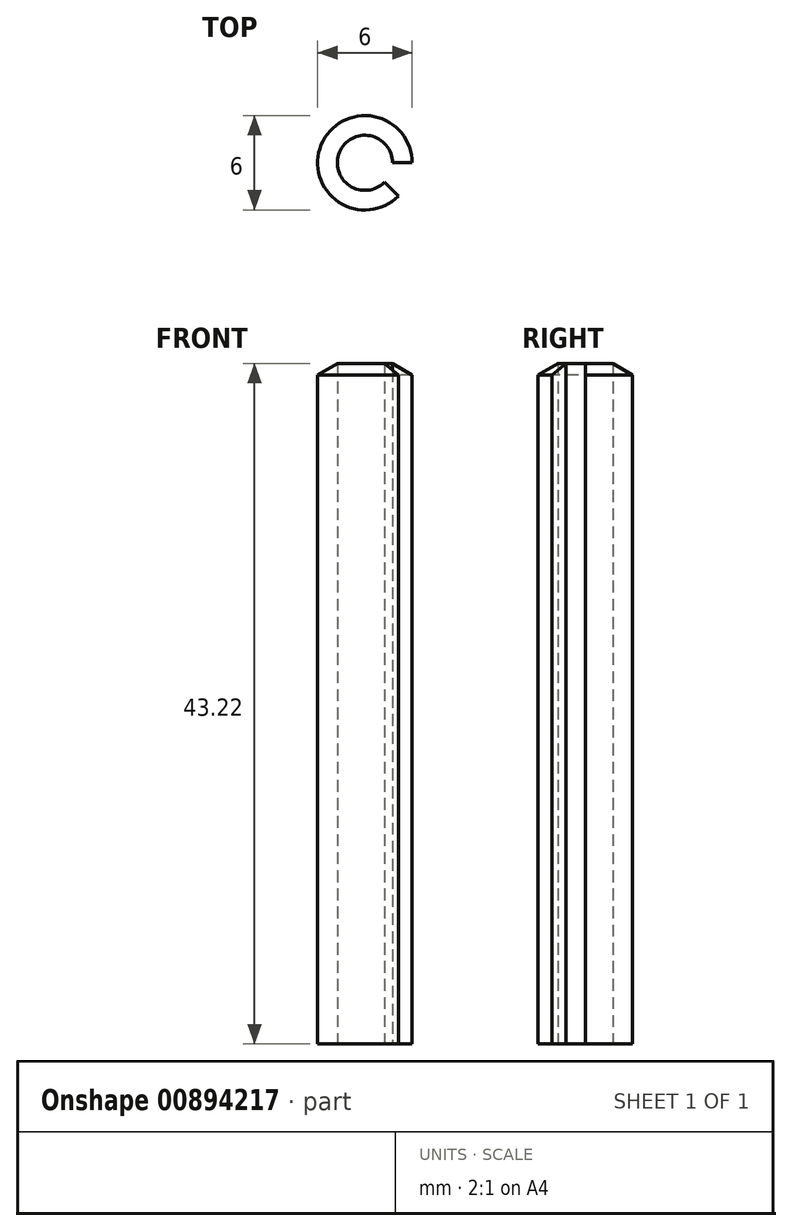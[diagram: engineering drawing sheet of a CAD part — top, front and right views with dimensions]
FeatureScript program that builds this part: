
annotation { "Feature Type Name" : "Feature", "Feature Type Description" : "" }
export const myFeature = defineFeature(function(context is Context, id is Id, definition is map)
    precondition{}
    {
        {
            var Q0;
            Q0=qCreatedBy(makeId("Top.planeOp"),FACE);
            var sketch = newSketch(context, id + "F0", { "sketchPlane" : qUnion([Q0])});
            skArc(sketch, "E0", {"start": v(3, 0) * mm, "mid": v(-2.77, 1.15) * mm, "end": v(2.12, -2.12) * mm});
            skLineSegment(sketch, "E1", {"start": v(2.12, -2.12) * mm, "end": v(1.24, -1.24) * mm});
            skLineSegment(sketch, "E2", {"start": v(3, 0) * mm, "end": v(1.75, 0) * mm});
            skArc(sketch, "E3", {"start": v(1.75, 0) * mm, "mid": v(-1.62, 0.67) * mm, "end": v(1.24, -1.24) * mm});
            skSolve(sketch);
        }
        {
            var Q0;
            Q0=makeQuery(id+"F0.imprint","IMPRINT",FACE,{"disambiguationData":[TD([[makeQuery(id+"F0.imprint","IMPRINT",EDGE,{"derivedFrom":sQuery(id+"F0.wireOp",EDGE,"E0")}),1.0]])]});
            extrude(context, id + "F1", {"entities" : qUnion([Q0]), "depth" : 43.5 * mm, "offsetDistance" : 25 * mm, "symmetric" : true});
        }
        {
            var Q0;
            Q0=makeQuery(id+"F1.opExtrude","CAP_EDGE",EDGE,{"disambiguationData":[OSD([sQuery(id+"F0.wireOp",EDGE,"E0")])],"isStart":false});
            chamfer(context, id + "F2", {"entities" : qUnion([Q0]), "chamferType" : ChamferType.OFFSET_ANGLE, "width" : 1 * mm, "oppositeDirection" : false, "angle" : 60 * degree, "tangentPropagation" : true});
        }
    });
